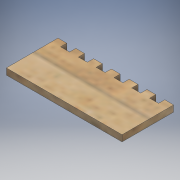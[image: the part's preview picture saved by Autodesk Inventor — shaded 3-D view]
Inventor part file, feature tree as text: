
AUTODESK INVENTOR PART (.ipt)
format: ipt  version: 2017 (Build 210142000, 142)  size: 147,456 bytes
history: native  units: mm
features: extrude x1, sketch x1
ambient origin geometry x8: Origin, YZ Plane, XZ Plane, XY Plane, X Axis, Y Axis, Z Axis, Center Point
bodies: Solid1 (feature_tree)
feature tree (2):
  extrude  "Extrusion1"  Depth=10.0mm
  sketch  "Sketch1"  dims[d4=10.0mm d5=10.0mm d6=10.0mm d9=10.0mm d12=10.0mm d13=10.0mm d14=10.0mm d15=10.0mm d16=10.0mm d17=10.0mm d18=10.0mm d19=10.0mm d20=7.0mm d21=0.0mm]
